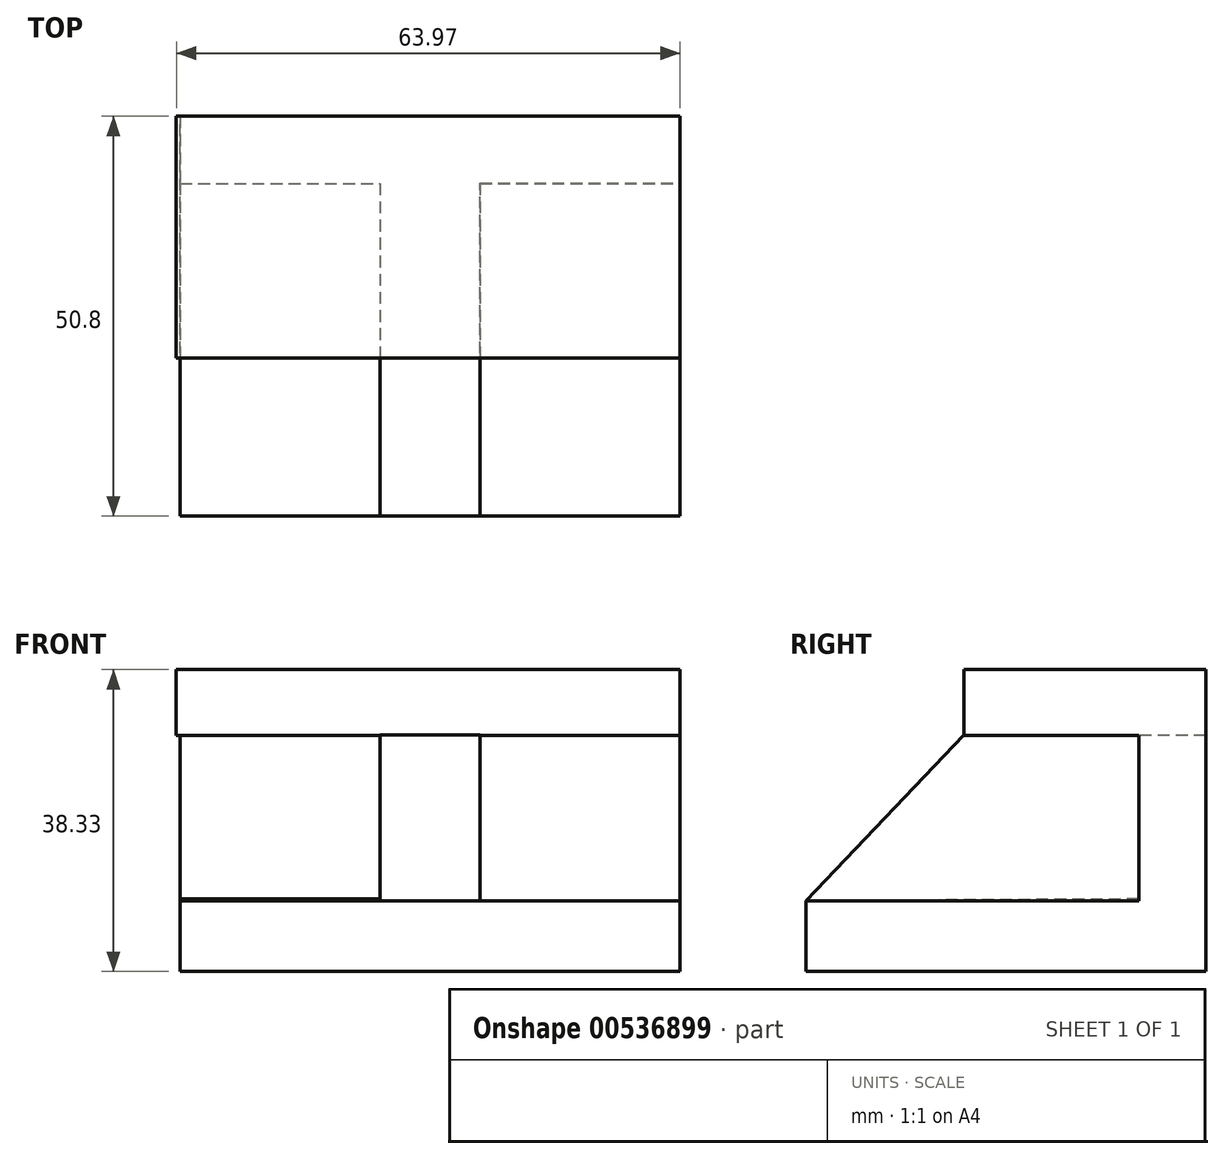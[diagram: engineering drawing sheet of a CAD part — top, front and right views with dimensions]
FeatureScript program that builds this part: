
annotation { "Feature Type Name" : "Feature", "Feature Type Description" : "" }
export const myFeature = defineFeature(function(context is Context, id is Id, definition is map)
    precondition{}
    {
        {
            var Q0;
            Q0=qCreatedBy(makeId("Front.planeOp"),FACE);
            var sketch = newSketch(context, id + "F0", { "sketchPlane" : qUnion([Q0])});
            skLineSegment(sketch, "E0.bottom", {"start": v(-4.07, 0) * mm, "end": v(-101.06, 0) * mm});
            skLineSegment(sketch, "E0.top", {"start": v(-4.07, -38.33) * mm, "end": v(-101.06, -38.33) * mm});
            skLineSegment(sketch, "E0.left", {"start": v(-4.07, 0) * mm, "end": v(-4.07, -38.33) * mm});
            skLineSegment(sketch, "E0.right", {"start": v(-101.06, 0) * mm, "end": v(-101.06, -38.33) * mm});
            skSolve(sketch);
        }
        {
            var Q0;
            Q0 = qSketchRegion(id + "F0", true);
            extrude(context, id + "F1", {"entities" : qUnion([Q0]), "depth" : 50.8 * mm, "offsetDistance" : 25.4 * mm});
        }
        {
            var Q0;
            Q0=makeQuery(id+"F1.opExtrude","SWEPT_FACE",FACE,{"disambiguationData":[OSD([sQuery(id+"F0.wireOp",EDGE,"E0.left")])]});
            var sketch = newSketch(context, id + "F2", { "sketchPlane" : qUnion([Q0])});
            skLineSegment(sketch, "E1", {"start": v(-50.8, -29.39) * mm, "end": v(-10.62, -29.39) * mm});
            skLineSegment(sketch, "E2", {"start": v(-10.62, -29.39) * mm, "end": v(-10.62, -8.34) * mm});
            skLineSegment(sketch, "E3", {"start": v(-10.62, -8.34) * mm, "end": v(-30.71, -8.34) * mm});
            skLineSegment(sketch, "E4", {"start": v(-30.71, -8.34) * mm, "end": v(-30.71, 0) * mm});
            skLineSegment(sketch, "E5", {"start": v(-30.71, 0) * mm, "end": v(0, 0) * mm});
            skLineSegment(sketch, "E6", {"start": v(0, 0) * mm, "end": v(0, -38.33) * mm});
            skLineSegment(sketch, "E7", {"start": v(0, -38.33) * mm, "end": v(-50.8, -38.33) * mm});
            skLineSegment(sketch, "E8", {"start": v(-50.8, -38.33) * mm, "end": v(-50.8, -29.39) * mm});
            skLineSegment(sketch, "E9", {"start": v(-50.8, -29.39) * mm, "end": v(-30.71, -8.34) * mm});
            skSolve(sketch);
        }
        {
            var Q0;
            {var subQ0=sQuery(id+"F2.wireOp",EDGE,"E4");Q0=makeQuery(id+"F2.imprint","IMPRINT",FACE,{"disambiguationData":[TD([[makeQuery(id+"F2.imprint","IMPRINT",EDGE,{"derivedFrom":subQ0}),1.0]])]});}
            extrude(context, id + "F3", {"entities" : qUnion([Q0]), "operationType" : NewBodyOperationType.REMOVE, "oppositeDirection" : true, "depth" : 101.6 * mm, "offsetDistance" : 25.4 * mm});
        }
        {
            var Q0;
            Q0=makeQuery(id+"F1.opExtrude","SWEPT_FACE",FACE,{"disambiguationData":[OSD([sQuery(id+"F0.wireOp",EDGE,"E0.left")])]});
            var sketch = newSketch(context, id + "F4", { "sketchPlane" : qUnion([Q0])});
            skLineSegment(sketch, "E10", {"start": v(-30.71, -8.34) * mm, "end": v(-8.53, -8.34) * mm});
            skLineSegment(sketch, "E11", {"start": v(-8.53, -8.34) * mm, "end": v(-8.53, -29.39) * mm});
            skLineSegment(sketch, "E12", {"start": v(-8.53, -29.39) * mm, "end": v(-50.8, -29.39) * mm});
            skSolve(sketch);
        }
        {
            var Q0;
            Q0 = qSketchRegion(id + "F4", true);
            var Q1;
            Q1=makeQuery(id+"F4.imprint","IMPRINT",FACE,{"disambiguationData":[TD([[makeQuery(id+"F4.imprint","IMPRINT",EDGE,{"derivedFrom":sQuery(id+"F4.wireOp",EDGE,"E10")}),-1.0]])]});
            extrude(context, id + "F5", {"entities" : qUnion([Q0, Q1]), "operationType" : NewBodyOperationType.REMOVE, "oppositeDirection" : true, "depth" : 25.4 * mm, "offsetDistance" : 25.4 * mm});
        }
        {
            var Q0;
            Q0=makeQuery(id+"F1.opExtrude","SWEPT_FACE",FACE,{"disambiguationData":[OSD([sQuery(id+"F0.wireOp",EDGE,"E0.right")])]});
            var sketch = newSketch(context, id + "F6", { "sketchPlane" : qUnion([Q0])});
            skLineSegment(sketch, "E13", {"start": v(30.71, -8.34) * mm, "end": v(10.05, -8.34) * mm});
            skLineSegment(sketch, "E14", {"start": v(10.05, -8.34) * mm, "end": v(10.05, -29.39) * mm});
            skLineSegment(sketch, "E15", {"start": v(10.05, -29.39) * mm, "end": v(50.8, -29.39) * mm});
            skSolve(sketch);
        }
        {
            var Q0;
            Q0=makeQuery(id+"F6.imprint","IMPRINT",FACE,{"disambiguationData":[TD([[makeQuery(id+"F6.imprint","IMPRINT",EDGE,{"derivedFrom":sQuery(id+"F6.wireOp",EDGE,"E13")}),1.0]])]});
            extrude(context, id + "F7", {"entities" : qUnion([Q0]), "operationType" : NewBodyOperationType.REMOVE, "oppositeDirection" : true, "depth" : 38.1 * mm, "offsetDistance" : 25.4 * mm});
        }
        {
            var Q0;
            Q0=makeQuery(id+"F5.boolean.opBoolean","COPY",FACE,{"derivedFrom":makeQuery(id+"F5.opExtrude","CAP_FACE",FACE,{"disambiguationData":[OSD([sQuery(id+"F2.wireOp",EDGE,"E9"),sQuery(id+"F4.wireOp",EDGE,"E10"),sQuery(id+"F4.wireOp",EDGE,"E11"),sQuery(id+"F4.wireOp",EDGE,"E12")])],"isStart":false})});
            extrude(context, id + "F8", {"entities" : qUnion([Q0]), "operationType" : NewBodyOperationType.REMOVE, "oppositeDirection" : true, "depth" : 38.1 * mm, "offsetDistance" : 25.4 * mm});
        }
        {
            var Q0;
            Q0=makeQuery(id+"F3.boolean.opBoolean","COPY",FACE,{"derivedFrom":makeQuery(id+"F3.opExtrude","SWEPT_FACE",FACE,{"disambiguationData":[OSD([sQuery(id+"F2.wireOp",EDGE,"E4")])]})});
            var sketch = newSketch(context, id + "F9", { "sketchPlane" : qUnion([Q0])});
            skLineSegment(sketch, "E16", {"start": v(-68.04, 0) * mm, "end": v(-68.04, -39.95) * mm});
            skSolve(sketch);
        }
        {
            var Q0;
            Q0 = qSketchRegion(id + "F9", true);
            var Q1;
            {var subQ1=sQuery(id+"F2.wireOp",EDGE,"E4");var subQ8=sQuery(id+"F0.wireOp",EDGE,"E0.right");var subQ11=makeQuery(id+"F3.boolean.opBoolean","INTERSECT",EDGE,{"derivedFrom":[makeQuery(id+"F1.opExtrude","SWEPT_FACE",FACE,{"disambiguationData":[OSD([subQ8])]}),makeQuery(id+"F3.opExtrude","SWEPT_FACE",FACE,{"disambiguationData":[OSD([subQ1])]})]});Q1=makeQuery(id+"F9.imprint","IMPRINT",FACE,{"disambiguationData":[TD([[makeQuery(id+"F9.imprint","IMPRINT",EDGE,{"derivedFrom":subQ11}),-1.0]])]});}
            extrude(context, id + "F10", {"entities" : qUnion([Q0, Q1]), "operationType" : NewBodyOperationType.REMOVE, "oppositeDirection" : true, "depth" : 47.75 * mm, "offsetDistance" : 25.4 * mm});
        }
        {
            var Q0;
            Q0=makeQuery(id+"F7.boolean.opBoolean","COPY",FACE,{"derivedFrom":makeQuery(id+"F7.opExtrude","SWEPT_FACE",FACE,{"disambiguationData":[OSD([sQuery(id+"F6.wireOp",EDGE,"E14")])]})});
            extrude(context, id + "F11", {"entities" : qUnion([Q0]), "operationType" : NewBodyOperationType.REMOVE, "oppositeDirection" : true, "depth" : 25.4 * mm, "offsetDistance" : 25.4 * mm});
        }
        {
            var Q0;
            {var subQ0=sQuery(id+"F6.wireOp",EDGE,"E15");var subQ1=sQuery(id+"F4.wireOp",EDGE,"E12");Q0=makeQuery(id+"F11.boolean.opBoolean","MERGE",FACE,{"derivedFrom":[makeQuery(id+"F8.boolean.opBoolean","MERGE",FACE,{"derivedFrom":[makeQuery(id+"F5.boolean.opBoolean","COPY",FACE,{"derivedFrom":makeQuery(id+"F5.opExtrude","SWEPT_FACE",FACE,{"disambiguationData":[OSD([subQ1])]})}),makeQuery(id+"F7.boolean.opBoolean","COPY",FACE,{"derivedFrom":makeQuery(id+"F7.opExtrude","SWEPT_FACE",FACE,{"disambiguationData":[OSD([subQ0])]})}),makeQuery(id+"F8.opExtrude","SWEPT_FACE",FACE,{"disambiguationData":[OSD([subQ1])]})]}),makeQuery(id+"F11.opExtrude","SWEPT_FACE",FACE,{"disambiguationData":[OSD([sQuery(id+"F6.wireOp",EDGE,"E14"),subQ0])]})]});}
            var sketch = newSketch(context, id + "F12", { "sketchPlane" : qUnion([Q0])});
            skLineSegment(sketch, "E17", {"start": v(-67.57, -8.53) * mm, "end": v(-67.57, -50.8) * mm});
            skSolve(sketch);
        }
        {
            var Q0;
            {var subQ9=sQuery(id+"F12.wireOp",EDGE,"E17");Q0=makeQuery(id+"F12.imprint","IMPRINT",FACE,{"disambiguationData":[TD([[makeQuery(id+"F12.imprint","IMPRINT",EDGE,{"derivedFrom":subQ9}),-1.0]])]});}
            extrude(context, id + "F13", {"entities" : qUnion([Q0]), "operationType" : NewBodyOperationType.REMOVE, "oppositeDirection" : true, "depth" : 25.4 * mm, "offsetDistance" : 25.4 * mm});
        }
        {
            var Q0;
            {var subQ0=sQuery(id+"F6.wireOp",EDGE,"E14");var subQ1=sQuery(id+"F4.wireOp",EDGE,"E12");var subQ2=sQuery(id+"F4.wireOp",EDGE,"E11");var subQ3=sQuery(id+"F4.wireOp",EDGE,"E10");var subQ4=sQuery(id+"F2.wireOp",EDGE,"E9");Q0=makeQuery(id+"F13.boolean.opBoolean","MERGE",FACE,{"derivedFrom":[makeQuery(id+"F11.boolean.opBoolean","COPY",FACE,{"derivedFrom":makeQuery(id+"F11.opExtrude","SWEPT_FACE",FACE,{"disambiguationData":[OSD([subQ4,subQ3,subQ2,subQ1,subQ0])]})}),makeQuery(id+"F13.opExtrude","SWEPT_FACE",FACE,{"disambiguationData":[OSD([subQ4,subQ3,subQ2,subQ1,subQ0,sQuery(id+"F12.wireOp",EDGE,"E17")])]})]});}
            var sketch = newSketch(context, id + "F14", { "sketchPlane" : qUnion([Q0])});
            skLineSegment(sketch, "E18", {"start": v(8.53, -8.34) * mm, "end": v(50.8, -29.39) * mm});
            skLineSegment(sketch, "E19", {"start": v(-325.51, -117.68) * mm, "end": v(-343.69, -96.47) * mm});
            skSolve(sketch);
        }
        {
            var Q0;
            Q0=makeQuery(id+"F14.imprint","IMPRINT",FACE,{"disambiguationData":[TD([[makeQuery(id+"F14.imprint","IMPRINT",EDGE,{"derivedFrom":sQuery(id+"F14.wireOp",EDGE,"E18")}),-1.0]])]});
            extrude(context, id + "F15", {"entities" : qUnion([Q0]), "operationType" : NewBodyOperationType.ADD, "oppositeDirection" : true, "depth" : 63.5 * mm, "offsetDistance" : 25.4 * mm});
        }
        {
            var Q0;
            Q0=makeQuery(id+"F15.boolean.opBoolean","MERGE",FACE,{"derivedFrom":[makeQuery(id+"F1.opExtrude","SWEPT_FACE",FACE,{"disambiguationData":[OSD([sQuery(id+"F0.wireOp",EDGE,"E0.left")])]}),makeQuery(id+"F15.opExtrude","CAP_FACE",FACE,{"disambiguationData":[OSD([sQuery(id+"F2.wireOp",EDGE,"E9"),sQuery(id+"F4.wireOp",EDGE,"E10"),sQuery(id+"F4.wireOp",EDGE,"E11"),sQuery(id+"F4.wireOp",EDGE,"E12"),sQuery(id+"F6.wireOp",EDGE,"E14"),sQuery(id+"F12.wireOp",EDGE,"E17"),sQuery(id+"F14.wireOp",EDGE,"E18")])],"isStart":false})]});
            var sketch = newSketch(context, id + "F16", { "sketchPlane" : qUnion([Q0])});
            skLineSegment(sketch, "E20", {"start": v(-50.8, -29.39) * mm, "end": v(-8.5, -29.39) * mm});
            skLineSegment(sketch, "E21", {"start": v(-8.5, -29.39) * mm, "end": v(-8.53, -8.34) * mm});
            skSolve(sketch);
        }
        {
            var Q0;
            Q0=makeQuery(id+"F16.imprint","IMPRINT",FACE,{"disambiguationData":[TD([[makeQuery(id+"F16.imprint","IMPRINT",EDGE,{"derivedFrom":sQuery(id+"F16.wireOp",EDGE,"E20")}),1.0]])]});
            extrude(context, id + "F17", {"entities" : qUnion([Q0]), "operationType" : NewBodyOperationType.REMOVE, "oppositeDirection" : true, "depth" : 25.4 * mm, "offsetDistance" : 25.4 * mm});
        }
        {
            var Q0;
            {var subQ0=sQuery(id+"F12.wireOp",EDGE,"E17");var subQ1=sQuery(id+"F6.wireOp",EDGE,"E14");var subQ2=sQuery(id+"F4.wireOp",EDGE,"E12");var subQ3=sQuery(id+"F4.wireOp",EDGE,"E11");var subQ4=sQuery(id+"F4.wireOp",EDGE,"E10");var subQ5=sQuery(id+"F2.wireOp",EDGE,"E9");Q0=makeQuery(id+"F15.boolean.opBoolean","MERGE",FACE,{"derivedFrom":[makeQuery(id+"F13.boolean.opBoolean","MERGE",FACE,{"derivedFrom":[makeQuery(id+"F11.boolean.opBoolean","COPY",FACE,{"derivedFrom":makeQuery(id+"F11.opExtrude","SWEPT_FACE",FACE,{"disambiguationData":[OSD([subQ5,subQ4,subQ3,subQ2,subQ1])]})}),makeQuery(id+"F13.opExtrude","SWEPT_FACE",FACE,{"disambiguationData":[OSD([subQ5,subQ4,subQ3,subQ2,subQ1,subQ0])]})]}),makeQuery(id+"F15.opExtrude","CAP_FACE",FACE,{"disambiguationData":[OSD([subQ5,subQ4,subQ3,subQ2,subQ1,subQ0,sQuery(id+"F14.wireOp",EDGE,"E18")])],"isStart":true})]});}
            var sketch = newSketch(context, id + "F18", { "sketchPlane" : qUnion([Q0])});
            skLineSegment(sketch, "E22", {"start": v(8.53, -8.34) * mm, "end": v(8.53, -29.14) * mm});
            skLineSegment(sketch, "E23", {"start": v(8.53, -29.14) * mm, "end": v(50.8, -29.39) * mm});
            skSolve(sketch);
        }
        {
            var Q0;
            Q0=makeQuery(id+"F18.imprint","IMPRINT",FACE,{"disambiguationData":[TD([[makeQuery(id+"F18.imprint","IMPRINT",EDGE,{"derivedFrom":sQuery(id+"F18.wireOp",EDGE,"E22")}),1.0]])]});
            extrude(context, id + "F19", {"entities" : qUnion([Q0]), "operationType" : NewBodyOperationType.REMOVE, "oppositeDirection" : true, "depth" : 25.4 * mm, "offsetDistance" : 25.4 * mm});
        }
        {
            var Q0;
            Q0=makeQuery(id+"F15.opExtrude","SWEPT_FACE",FACE,{"disambiguationData":[OSD([sQuery(id+"F14.wireOp",EDGE,"E18")])]});
            extrude(context, id + "F20", {"entities" : qUnion([Q0]), "operationType" : NewBodyOperationType.ADD, "depth" : 9.9 * mm, "offsetDistance" : 25.4 * mm});
        }
        {
            var Q0;
            {var subQ0=sQuery(id+"F14.wireOp",EDGE,"E18");Q0=makeQuery(id+"F20.boolean.opBoolean","MERGE",FACE,{"derivedFrom":[makeQuery(id+"F17.boolean.opBoolean","COPY",FACE,{"derivedFrom":makeQuery(id+"F17.opExtrude","CAP_FACE",FACE,{"disambiguationData":[OSD([subQ0,sQuery(id+"F16.wireOp",EDGE,"E20"),sQuery(id+"F16.wireOp",EDGE,"E21")])],"isStart":false})}),makeQuery(id+"F20.opExtrude","SWEPT_FACE",FACE,{"disambiguationData":[OSD([subQ0]),TDD([makeQuery(id+"F17.boolean.opBoolean","COPY",EDGE,{"derivedFrom":makeQuery(id+"F17.opExtrude","CAP_EDGE",EDGE,{"disambiguationData":[OSD([subQ0])],"isStart":false})})])]})]});}
            var sketch = newSketch(context, id + "F21", { "sketchPlane" : qUnion([Q0])});
            skLineSegment(sketch, "E24", {"start": v(-50.8, -29.39) * mm, "end": v(-30.71, -8.32) * mm});
            skSolve(sketch);
        }
        {
            var Q0;
            Q0=makeQuery(id+"F21.imprint","IMPRINT",FACE,{"disambiguationData":[TD([[makeQuery(id+"F21.imprint","IMPRINT",EDGE,{"derivedFrom":sQuery(id+"F21.wireOp",EDGE,"E24")}),1.0]])]});
            extrude(context, id + "F22", {"entities" : qUnion([Q0]), "operationType" : NewBodyOperationType.REMOVE, "oppositeDirection" : true, "depth" : 25.4 * mm, "offsetDistance" : 25.4 * mm});
        }
        {
            var Q0;
            {var subQ0=sQuery(id+"F14.wireOp",EDGE,"E18");Q0=makeQuery(id+"F20.boolean.opBoolean","SPLIT",FACE,{"disambiguationData":[TD([makeQuery(id+"F1.opExtrude","SWEPT_FACE",FACE,{"disambiguationData":[OSD([sQuery(id+"F0.wireOp",EDGE,"E0.bottom")])]})])],"derivedFrom":makeQuery(id+"F20.opExtrude","CAP_FACE",FACE,{"disambiguationData":[OSD([subQ0])],"isStart":false})});}
            extrude(context, id + "F23", {"entities" : qUnion([Q0]), "operationType" : NewBodyOperationType.ADD, "oppositeDirection" : true, "depth" : 0.25 * mm, "offsetDistance" : 25.4 * mm});
        }
        {
            var Q0;
            {var subQ0=sQuery(id+"F14.wireOp",EDGE,"E18");Q0=makeQuery(id+"F20.boolean.opBoolean","SPLIT",FACE,{"derivedFrom":makeQuery(id+"F20.opExtrude","SWEPT_FACE",FACE,{"disambiguationData":[OSD([subQ0]),TDD([makeQuery(id+"F17.boolean.opBoolean","COPY",EDGE,{"derivedFrom":makeQuery(id+"F17.opExtrude","CAP_EDGE",EDGE,{"disambiguationData":[OSD([subQ0])],"isStart":false})})])]})});}
            extrude(context, id + "F24", {"entities" : qUnion([Q0]), "operationType" : NewBodyOperationType.REMOVE, "oppositeDirection" : true, "depth" : 25.4 * mm, "offsetDistance" : 25.4 * mm});
        }
    });
